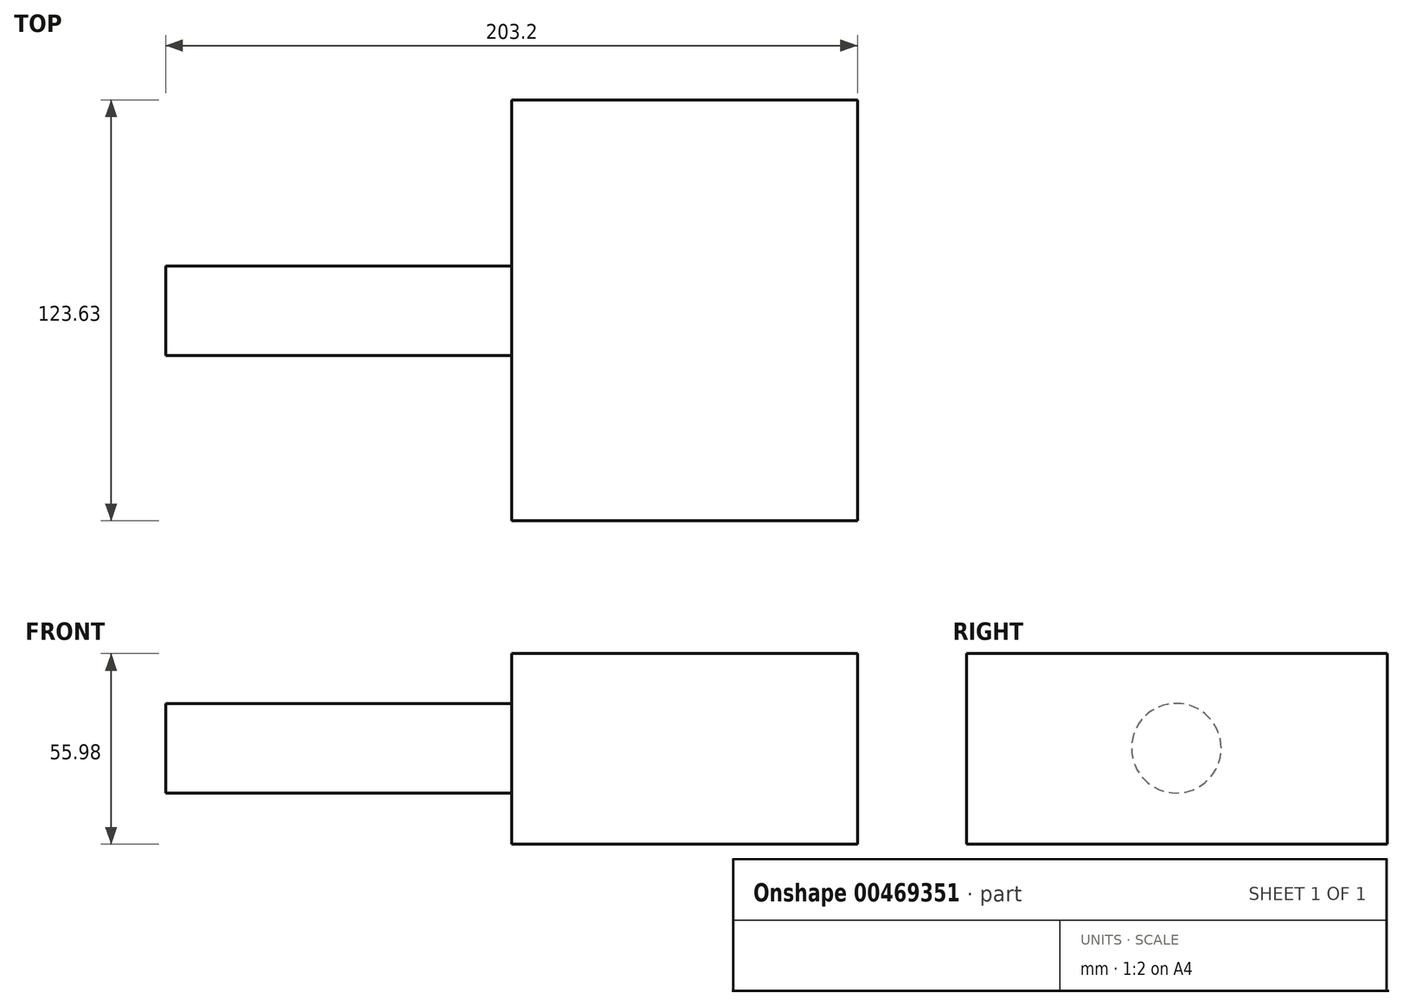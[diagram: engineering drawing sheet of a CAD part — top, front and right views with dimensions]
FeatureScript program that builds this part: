
annotation { "Feature Type Name" : "Feature", "Feature Type Description" : "" }
export const myFeature = defineFeature(function(context is Context, id is Id, definition is map)
    precondition{}
    {
        {
            var Q0;
            Q0=qCreatedBy(makeId("Right.planeOp"),FACE);
            var sketch = newSketch(context, id + "F0", { "sketchPlane" : qUnion([Q0])});
            skLineSegment(sketch, "E0.bottom", {"start": v(-100.5, -3.2) * mm, "end": v(23.14, -3.2) * mm});
            skLineSegment(sketch, "E0.top", {"start": v(-100.5, 52.78) * mm, "end": v(23.14, 52.78) * mm});
            skLineSegment(sketch, "E0.left", {"start": v(-100.5, -3.2) * mm, "end": v(-100.5, 52.78) * mm});
            skLineSegment(sketch, "E0.right", {"start": v(23.14, -3.2) * mm, "end": v(23.14, 52.78) * mm});
            skSolve(sketch);
        }
        {
            var Q0;
            Q0=makeQuery(id+"F0.imprint","IMPRINT",FACE,{"disambiguationData":[TD([[makeQuery(id+"F0.imprint","IMPRINT",EDGE,{"derivedFrom":sQuery(id+"F0.wireOp",EDGE,"E0.bottom")}),1.0]])]});
            extrude(context, id + "F1", {"entities" : qUnion([Q0]), "depth" : 101.6 * mm});
        }
        {
            var Q0;
            Q0=makeQuery(id+"F1.opExtrude","CAP_FACE",FACE,{"disambiguationData":[OSD([sQuery(id+"F0.wireOp",EDGE,"E0.bottom"),sQuery(id+"F0.wireOp",EDGE,"E0.top"),sQuery(id+"F0.wireOp",EDGE,"E0.left"),sQuery(id+"F0.wireOp",EDGE,"E0.right")])],"isStart":false});
            var sketch = newSketch(context, id + "F2", { "sketchPlane" : qUnion([Q0])});
            skCircle(sketch, "E1", {"center": v(-38.83, 25) * mm, "radius": 13.16 * mm});
            skSolve(sketch);
        }
        {
            var Q0;
            Q0 = qSketchRegion(id + "F2", true);
            extrude(context, id + "F3", {"entities" : qUnion([Q0]), "operationType" : NewBodyOperationType.ADD, "depth" : -203.2 * mm, "hasSecondDirection" : true, "secondDirectionOppositeDirection" : true, "secondDirectionDepth" : 25.4 * mm});
        }
    });
